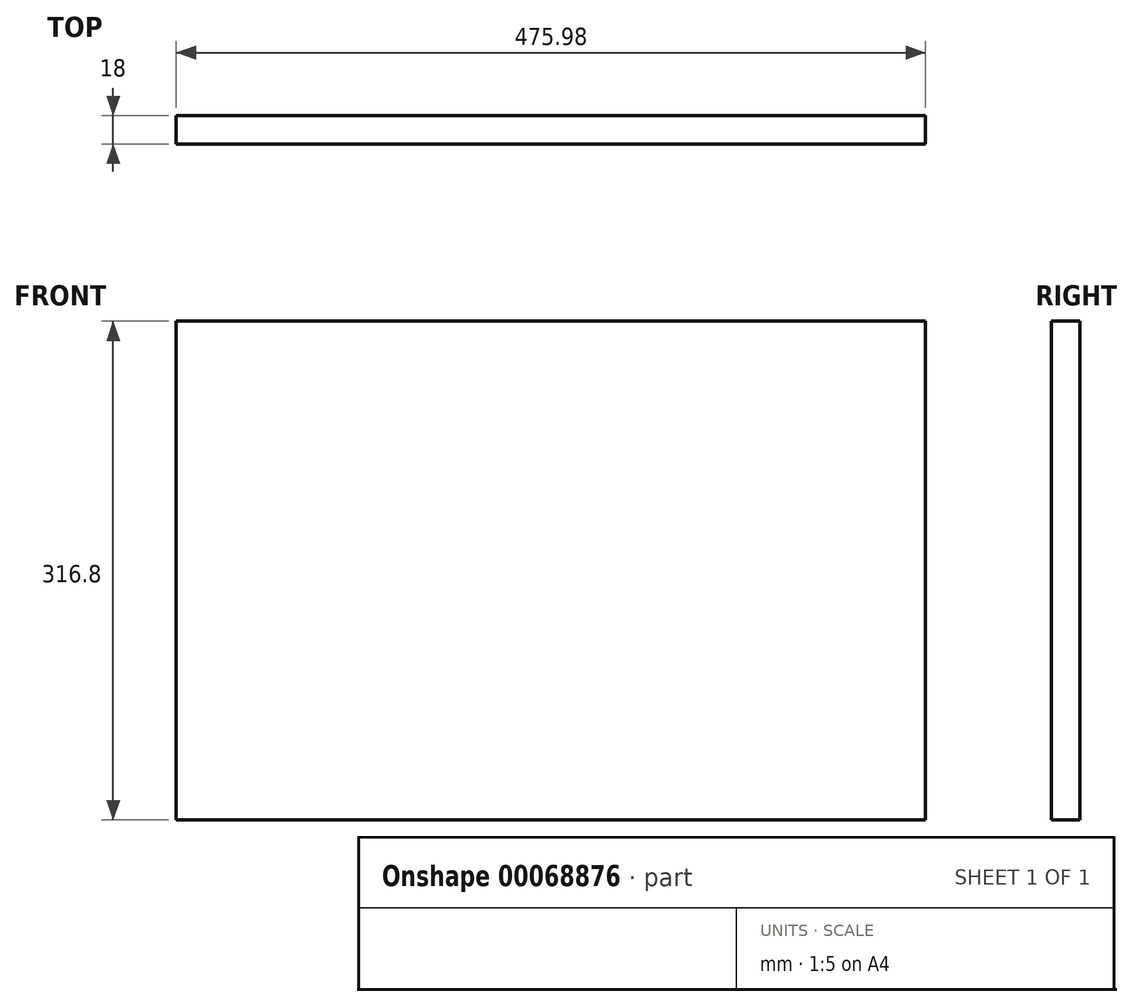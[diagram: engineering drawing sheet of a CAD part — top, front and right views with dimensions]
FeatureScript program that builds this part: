
annotation { "Feature Type Name" : "Feature", "Feature Type Description" : "" }
export const myFeature = defineFeature(function(context is Context, id is Id, definition is map)
    precondition{}
    {
        {
            assignVariable(context, id + "F0", {"name" : "MaterialThickness", "anyValue" : 18 * mm});
        }
        {
            var Q0;
            Q0=qCreatedBy(makeId("Front.planeOp"),FACE);
            var sketch = newSketch(context, id + "F1", { "sketchPlane" : qUnion([Q0])});
            skLineSegment(sketch, "E0.bottom", {"start": v(-148.72, 118.75) * mm, "end": v(327.26, 118.75) * mm});
            skLineSegment(sketch, "E0.top", {"start": v(-148.72, -198.05) * mm, "end": v(327.26, -198.05) * mm});
            skLineSegment(sketch, "E0.left", {"start": v(-148.72, 118.75) * mm, "end": v(-148.72, -198.05) * mm});
            skLineSegment(sketch, "E0.right", {"start": v(327.26, 118.75) * mm, "end": v(327.26, -198.05) * mm});
            skSolve(sketch);
        }
        {
            var Q0;
            Q0 = qSketchRegion(id + "F1", true);
            extrude(context, id + "F2", {"entities" : qUnion([Q0]), "depth" : getVariable(context, 'MaterialThickness')});
        }
    });
